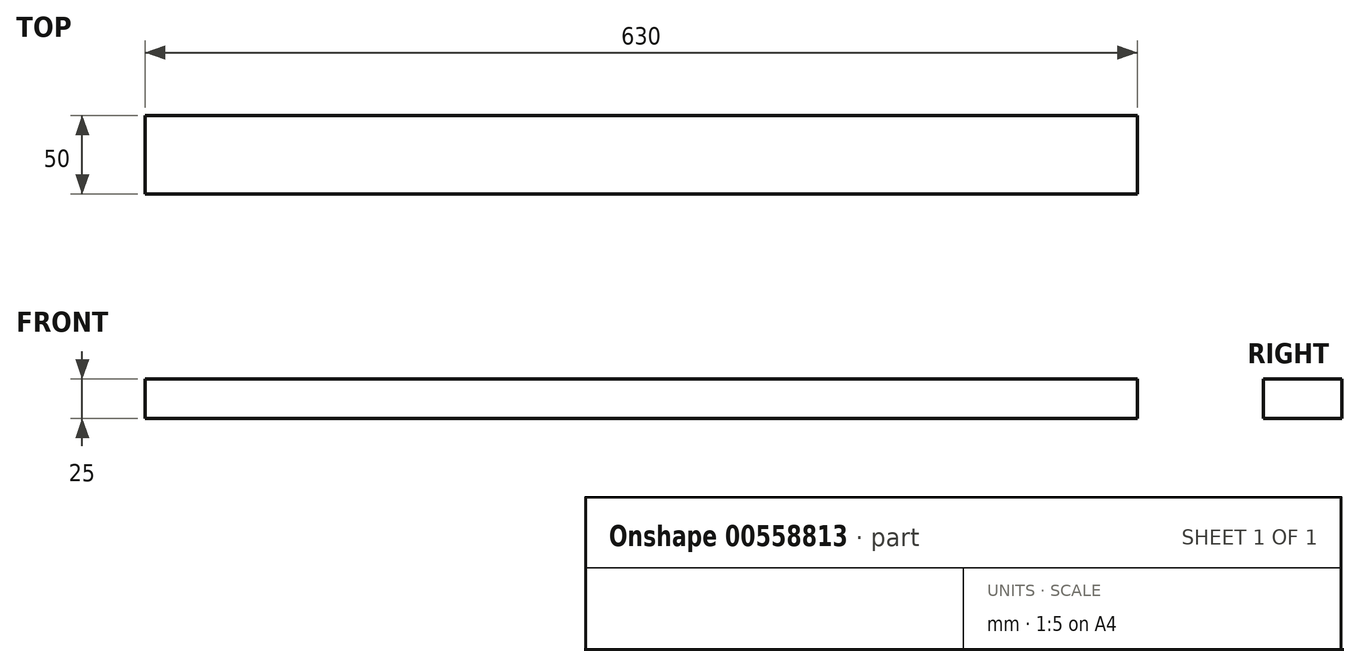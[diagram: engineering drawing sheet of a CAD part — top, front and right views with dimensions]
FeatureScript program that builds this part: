
annotation { "Feature Type Name" : "Feature", "Feature Type Description" : "" }
export const myFeature = defineFeature(function(context is Context, id is Id, definition is map)
    precondition{}
    {
        {
            var Q0;
            Q0=qCreatedBy(makeId("Top.planeOp"),FACE);
            var sketch = newSketch(context, id + "F0", { "sketchPlane" : qUnion([Q0])});
            skLineSegment(sketch, "E0.bottom", {"start": v(-315, 25) * mm, "end": v(315, 25) * mm});
            skLineSegment(sketch, "E0.top", {"start": v(-315, -25) * mm, "end": v(315, -25) * mm});
            skLineSegment(sketch, "E0.left", {"start": v(-315, 25) * mm, "end": v(-315, -25) * mm});
            skLineSegment(sketch, "E0.right", {"start": v(315, 25) * mm, "end": v(315, -25) * mm});
            skPoint(sketch, "E0.middle", {"position": v(0, 0) * mm});
            skSolve(sketch);
        }
        {
            var Q0;
            Q0 = qSketchRegion(id + "F0", true);
            extrude(context, id + "F1", {"entities" : qUnion([Q0]), "endBound" : BoundingType.SYMMETRIC, "depth" : 25 * mm, "offsetDistance" : 25 * mm});
        }
    });
